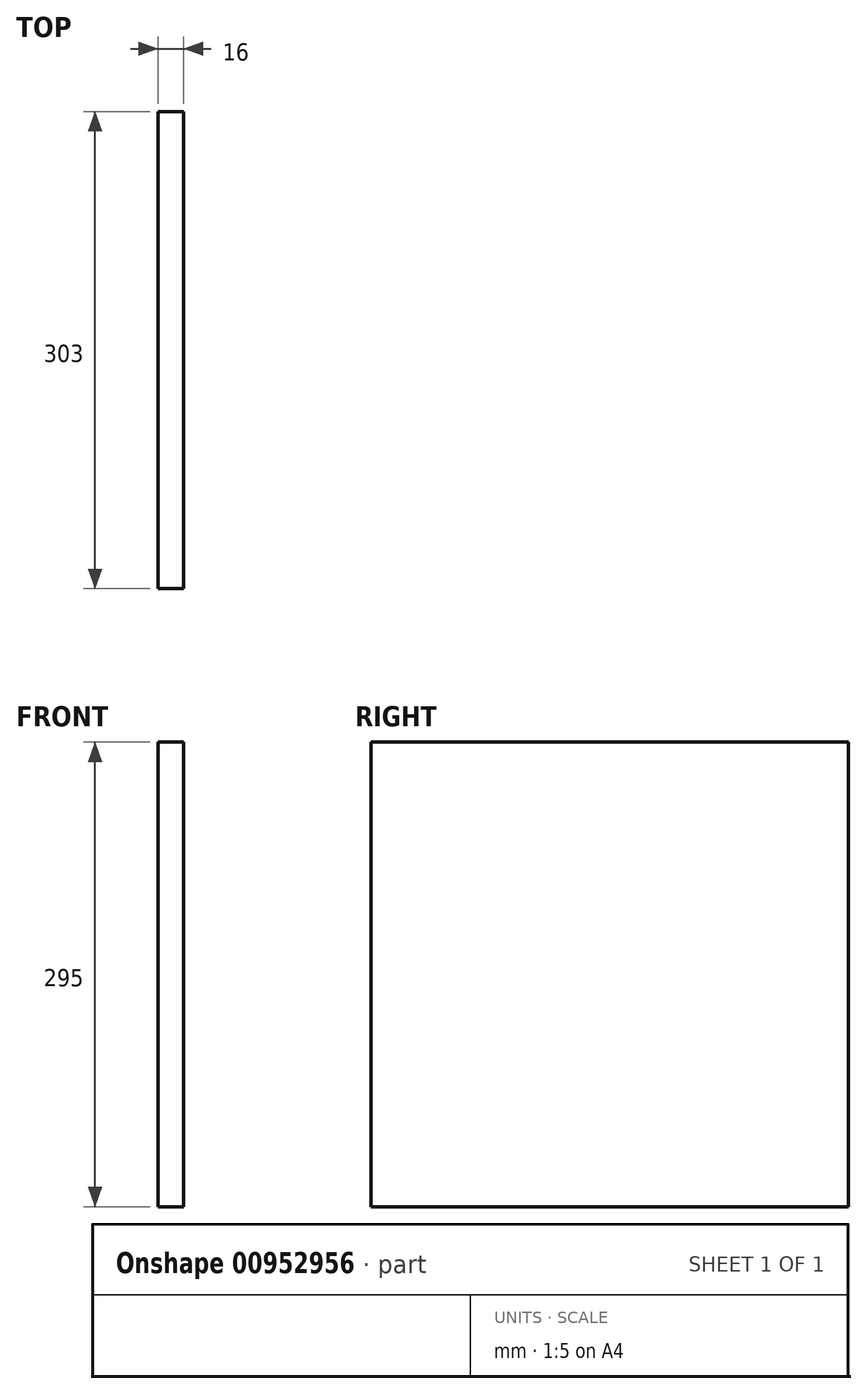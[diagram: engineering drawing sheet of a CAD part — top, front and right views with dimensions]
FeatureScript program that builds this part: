
annotation { "Feature Type Name" : "Feature", "Feature Type Description" : "" }
export const myFeature = defineFeature(function(context is Context, id is Id, definition is map)
    precondition{}
    {
        {
            var Q0;
            Q0=qCreatedBy(makeId("Right.planeOp"),FACE);
            var sketch = newSketch(context, id + "F0", { "sketchPlane" : qUnion([Q0])});
            skLineSegment(sketch, "E0.bottom", {"start": v(-172.8, 138.72) * mm, "end": v(130.2, 138.72) * mm});
            skLineSegment(sketch, "E0.top", {"start": v(-172.8, -156.28) * mm, "end": v(130.2, -156.28) * mm});
            skLineSegment(sketch, "E0.left", {"start": v(-172.8, 138.72) * mm, "end": v(-172.8, -156.28) * mm});
            skLineSegment(sketch, "E0.right", {"start": v(130.2, 138.72) * mm, "end": v(130.2, -156.28) * mm});
            skSolve(sketch);
        }
        {
            var Q0;
            Q0 = qSketchRegion(id + "F0", true);
            extrude(context, id + "F1", {"entities" : qUnion([Q0]), "depth" : 16 * mm, "offsetDistance" : 25 * mm});
        }
    });
